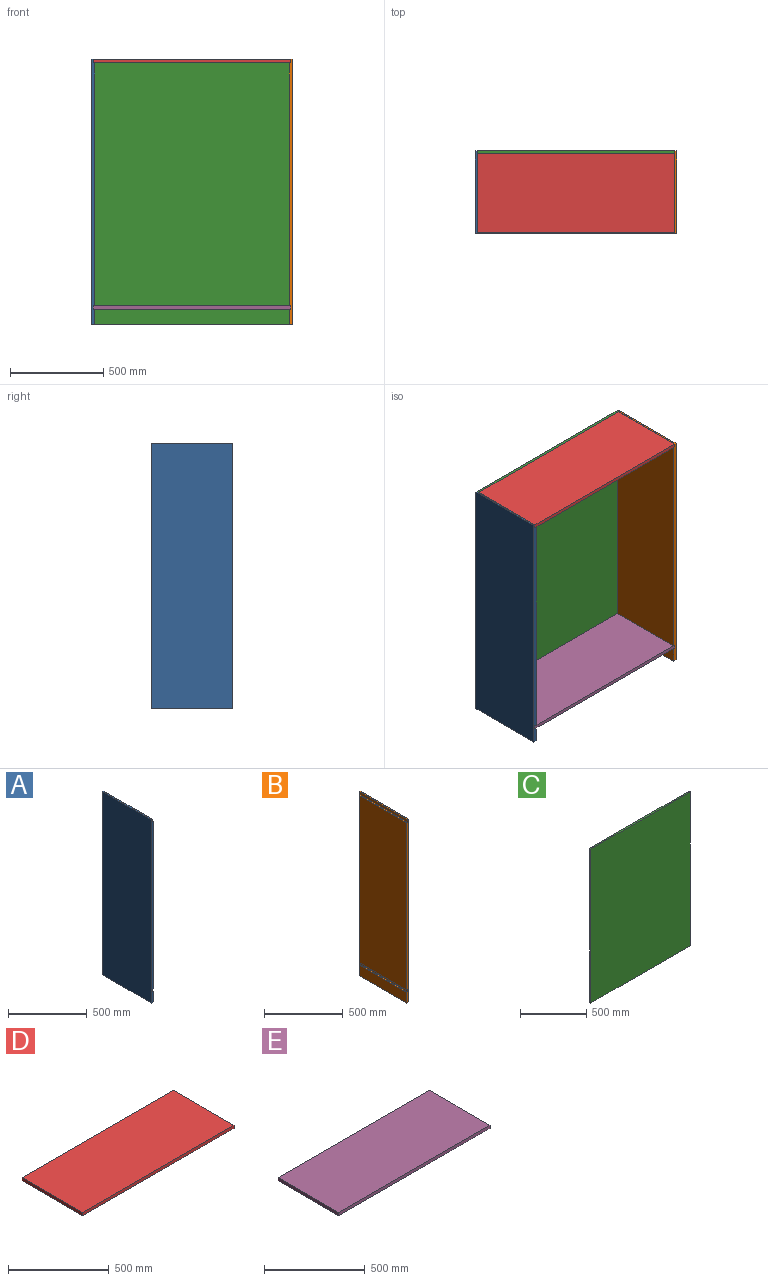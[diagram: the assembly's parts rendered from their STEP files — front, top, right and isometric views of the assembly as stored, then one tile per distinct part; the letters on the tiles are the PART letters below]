
ASSEMBLY  parts=5 mates=4
PART A: 13 faces, bbox 19.1x438.2x1422.4 mm
  f0: plane 438.15x19.05mm, normal (0,0,-1), area 8225.8mm2, adj f1,f3,f4,f6,f9,f12
  f1: plane 1422.4x9.53mm, normal (0,1,0), area 13548.4mm2, adj f0,f2,f6,f9
  f2: plane 438.15x9.53mm, normal (0,0,1), area 4173.4mm2, adj f1,f4,f6,f9
  f3: plane 425.45x82.55mm, normal (1,0,0), area 35120.9mm2, adj f0,f4,f7,f12
  f4: plane 1422.4x19.05mm, normal (0,-1,0), area 26733.8mm2, adj f0,f2,f3,f5,f6,f7,f8,f9
  f5: plane 1301.75x425.45mm, normal (1,0,0), area 553829.5mm2, adj f4,f8,f10,f11
  f6: plane 1422.4x438.15mm, normal (-1,0,0), area 623224.6mm2, adj f0,f1,f2,f4
  f7: plane 425.45x9.53mm, normal (0,0,1), area 4052.4mm2, adj f3,f4,f9,f12
  f8: plane 425.45x9.53mm, normal (0,0,-1), area 4052.4mm2, adj f4,f5,f9,f11
  f9: plane 1422.4x438.15mm, normal (1,0,0), area 34274.1mm2, adj f0,f1,f2,f4,f7,f8,f10,f11
  f10: plane 425.45x9.53mm, normal (0,0,1), area 4052.4mm2, adj f4,f5,f9,f11
  f11: plane 1301.75x9.53mm, normal (0,1,0), area 12399.2mm2, adj f5,f8,f9,f10
  f12: plane 82.55x9.53mm, normal (0,1,0), area 786.3mm2, adj f0,f3,f7,f9
PART B: 13 faces, bbox 19.1x438.2x1422.4 mm
  f0: plane 1422.4x9.53mm, normal (0,1,0), area 13548.4mm2, adj f3,f4,f6,f9
  f1: plane 1422.4x19.05mm, normal (0,-1,0), area 26733.8mm2, adj f2,f3,f4,f5,f6,f7,f8,f9
  f2: plane 425.45x82.55mm, normal (-1,0,0), area 35120.9mm2, adj f1,f4,f7,f12
  f3: plane 438.15x9.53mm, normal (0,0,1), area 4173.4mm2, adj f0,f1,f6,f9
  f4: plane 438.15x19.05mm, normal (0,0,-1), area 8225.8mm2, adj f0,f1,f2,f6,f9,f12
  f5: plane 1301.75x425.45mm, normal (-1,0,0), area 553829.5mm2, adj f1,f8,f10,f11
  f6: plane 1422.4x438.15mm, normal (1,0,0), area 623224.6mm2, adj f0,f1,f3,f4
  f7: plane 425.45x9.53mm, normal (0,0,1), area 4052.4mm2, adj f1,f2,f9,f12
  f8: plane 425.45x9.53mm, normal (0,0,-1), area 4052.4mm2, adj f1,f5,f9,f11
  f9: plane 1422.4x438.15mm, normal (-1,0,0), area 34274.1mm2, adj f0,f1,f3,f4,f7,f8,f10,f11
  f10: plane 425.45x9.53mm, normal (0,0,1), area 4052.4mm2, adj f1,f5,f9,f11
  f11: plane 1301.75x9.53mm, normal (0,1,0), area 12399.2mm2, adj f5,f8,f9,f10
  f12: plane 82.55x9.53mm, normal (0,1,0), area 786.3mm2, adj f2,f4,f7,f9
PART C: 6 faces, bbox 1060.5x12.7x1422.4 mm
  f0: plane 1422.4x12.7mm, normal (-1,0,0), area 18064.5mm2, adj f1,f3,f4,f5
  f1: plane 1422.4x1060.45mm, normal (0,-1,0), area 1508384.1mm2, adj f0,f2,f4,f5
  f2: plane 1422.4x12.7mm, normal (1,0,0), area 18064.5mm2, adj f1,f3,f4,f5
  f3: plane 1422.4x1060.45mm, normal (0,1,0), area 1508384.1mm2, adj f0,f2,f4,f5
  f4: plane 1060.45x12.7mm, normal (0,0,-1), area 13467.7mm2, adj f0,f1,f2,f3
  f5: plane 1060.45x12.7mm, normal (0,0,1), area 13467.7mm2, adj f0,f1,f2,f3
PART D: 6 faces, bbox 1060.5x425.5x19.1 mm
  f0: plane 1060.45x425.45mm, normal (0,0,1), area 451168.5mm2, adj f1,f3,f4,f5
  f1: plane 425.45x19.05mm, normal (-1,0,0), area 8104.8mm2, adj f0,f2,f4,f5
  f2: plane 1060.45x425.45mm, normal (0,0,-1), area 451168.5mm2, adj f1,f3,f4,f5
  f3: plane 425.45x19.05mm, normal (1,0,0), area 8104.8mm2, adj f0,f2,f4,f5
  f4: plane 1060.45x19.05mm, normal (0,-1,0), area 20201.6mm2, adj f0,f1,f2,f3
  f5: plane 1060.45x19.05mm, normal (0,1,0), area 20201.6mm2, adj f0,f1,f2,f3
PART E: 6 faces, bbox 1060.5x425.5x19.1 mm
  f0: plane 425.45x19.05mm, normal (1,0,0), area 8104.8mm2, adj f2,f3,f4,f5
  f1: plane 425.45x19.05mm, normal (-1,0,0), area 8104.8mm2, adj f2,f3,f4,f5
  f2: plane 1060.45x425.45mm, normal (0,0,-1), area 451168.5mm2, adj f0,f1,f4,f5
  f3: plane 1060.45x425.45mm, normal (0,0,1), area 451168.5mm2, adj f0,f1,f4,f5
  f4: plane 1060.45x19.05mm, normal (0,-1,0), area 20201.6mm2, adj f0,f1,f2,f3
  f5: plane 1060.45x19.05mm, normal (0,1,0), area 20201.6mm2, adj f0,f1,f2,f3
PLACE A t=(-254.77,-430.67,118.67)mm fixed
PLACE B t=(-254.77,-430.67,118.67)mm
PLACE C t=(-254.77,-430.67,118.67)mm
PLACE D t=(-254.77,-430.67,118.67)mm
PLACE E t=(-254.77,-430.67,118.67)mm
MATE fastened D.f5 <-> C.f1  axis (0,1,0) through (-794.52,-5.22,1541.07)mm
MATE fastened A.f7 <-> E.f2  axis (0,0,1) through (-1324.75,-217.95,201.22)mm
MATE fastened D.f2 <-> B.f10  axis (0,0,-1) through (-264.3,-217.95,1522.02)mm
MATE fastened A.f10 <-> D.f2  axis (0,0,1) through (-1324.75,-217.95,1522.02)mm
